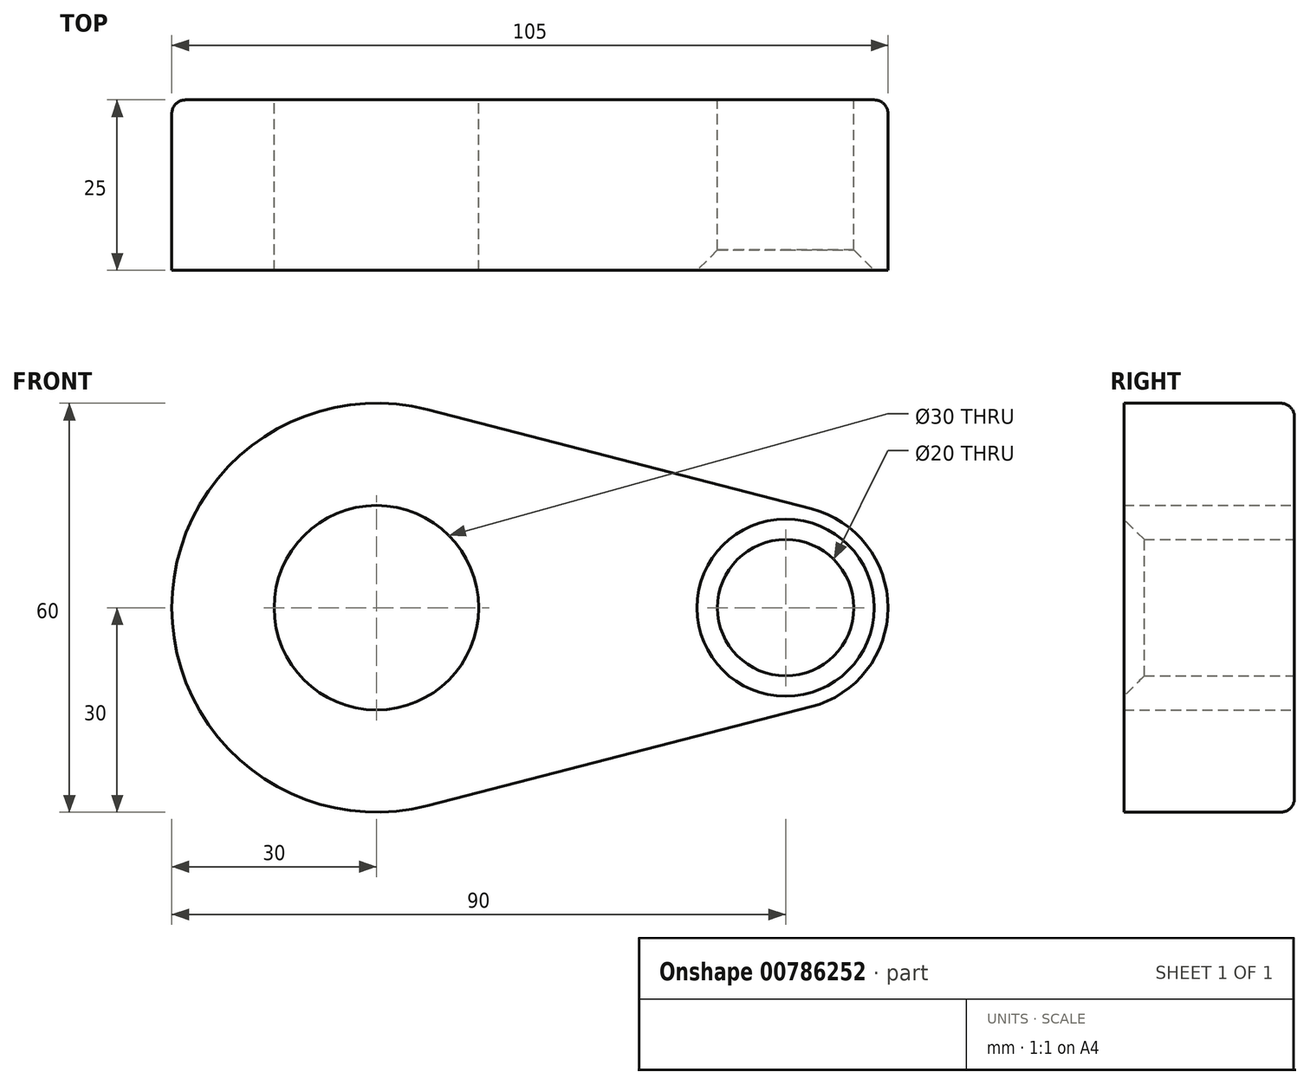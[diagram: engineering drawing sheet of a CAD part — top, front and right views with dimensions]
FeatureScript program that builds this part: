
annotation { "Feature Type Name" : "Feature", "Feature Type Description" : "" }
export const myFeature = defineFeature(function(context is Context, id is Id, definition is map)
    precondition{}
    {
        {
            var Q0;
            Q0=qCreatedBy(makeId("Front.planeOp"),FACE);
            var sketch = newSketch(context, id + "F0", { "sketchPlane" : qUnion([Q0])});
            skCircle(sketch, "E0", {"center": v(0, 0) * mm, "radius": 30 * mm});
            skCircle(sketch, "E1", {"center": v(60, 0) * mm, "radius": 15 * mm});
            skLineSegment(sketch, "E2", {"start": v(7.5, 29.05) * mm, "end": v(63.75, 14.52) * mm});
            skLineSegment(sketch, "E3", {"start": v(7.5, -29.05) * mm, "end": v(63.75, -14.52) * mm});
            skCircle(sketch, "E4", {"center": v(60, 0) * mm, "radius": 10 * mm});
            skCircle(sketch, "E5", {"center": v(0, 0) * mm, "radius": 15 * mm});
            skSolve(sketch);
        }
        {
            var Q0;
            Q0 = qSketchRegion(id + "F0", true);
            extrude(context, id + "F1", {"entities" : qUnion([Q0]), "depth" : 25 * mm, "offsetDistance" : 25 * mm});
        }
        {
            var Q0;
            Q0=makeQuery(id+"F2.opExtrude","CAP_EDGE",EDGE,{"disambiguationData":[OSD([sQuery(id+"F0.wireOp",EDGE,"E0")])],"isStart":false});
            var Q1;
            Q1=makeQuery(id+"F1.opExtrude","CAP_EDGE",EDGE,{"disambiguationData":[OSD([sQuery(id+"F0.wireOp",EDGE,"E0")])],"isStart":true});
            var Q2;
            Q2=makeQuery(id+"F1.opExtrude","CAP_EDGE",EDGE,{"disambiguationData":[OSD([sQuery(id+"F0.wireOp",EDGE,"E3")])],"isStart":true});
            var Q3;
            Q3=makeQuery(id+"F1.opExtrude","CAP_EDGE",EDGE,{"disambiguationData":[OSD([sQuery(id+"F0.wireOp",EDGE,"E1")])],"isStart":true});
            var Q4;
            Q4=makeQuery(id+"F1.opExtrude","CAP_EDGE",EDGE,{"disambiguationData":[OSD([sQuery(id+"F0.wireOp",EDGE,"E2")])],"isStart":true});
            fillet(context, id + "F3", {"entities" : qUnion([Q0, Q1, Q2, Q3, Q4]), "radius" : 2 * mm, "tangentPropagation" : true, "allowEdgeOverflow" : false});
        }
        {
            var Q0;
            Q0=makeQuery(id+"F2.opExtrude","CAP_EDGE",EDGE,{"disambiguationData":[OSD([sQuery(id+"F0.wireOp",EDGE,"E5")])],"isStart":false});
            var Q1;
            Q1=makeQuery(id+"F1.opExtrude","CAP_EDGE",EDGE,{"disambiguationData":[OSD([sQuery(id+"F0.wireOp",EDGE,"E4")])],"isStart":false});
            chamfer(context, id + "F4", {"entities" : qUnion([Q0, Q1]), "width" : 3 * mm, "tangentPropagation" : true});
        }
    });
